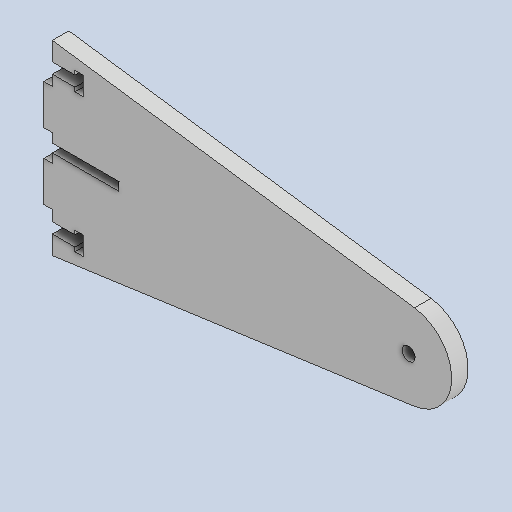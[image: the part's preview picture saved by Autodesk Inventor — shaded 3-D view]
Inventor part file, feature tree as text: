
AUTODESK INVENTOR PART (.ipt)
format: ipt  version: 2022 (Build 260153000, 153)  size: 166,400 bytes
history: native  units: mm
features: reference x8, other x5, extrude x3, sketch x3
ambient origin geometry x8: Origin, YZ Plane, XZ Plane, XY Plane, X Axis, Y Axis, Z Axis, Center Point
bodies: Solid1 (feature_tree)
feature tree (19):
  extrude  "Extrusion1"  Depth=150.0mm
  extrude  "Extrusion2"  Depth=136.046958mm
  extrude  "Extrusion3"  Depth=6.2mm TaperAngle=0.0deg
  sketch  "Sketch2"  dims[d0=5.0mm d1=150.0mm]
  reference  "Reference1"
  reference  "Reference2"
  reference  "Reference3"
  reference  "Reference4"
  reference  "Reference5"
  reference  "Reference6"
  reference  "Reference7"
  sketch  "Sketch4"  dims[d2=35.0mm d3=136.046958mm]
  sketch  "Sketch5"  dims[d4=32.066454mm d5=6.2mm d6=0.0mm d7=3.2mm d8=15.0mm d9=15.0mm d10=1.6mm d11=25.0mm d12=10.0mm d13=0.0mm d14=8.5mm d15=4.0mm d16=7.0mm d17=3.5mm d18=3.2mm d19=6.2mm d20=0.0mm]
  reference  "Reference8"
  other  "<userpath>\OneDrive\Escritorio\Mini_Proyecto_Diseno\Diseno_18012\Modelo_MPD\Carril.iam"
  other  "Carril.iam"
  other  "Eje_Carril:1"
  other  "Assembly_Final.iam"
  other  "Base_proyecto:1"
